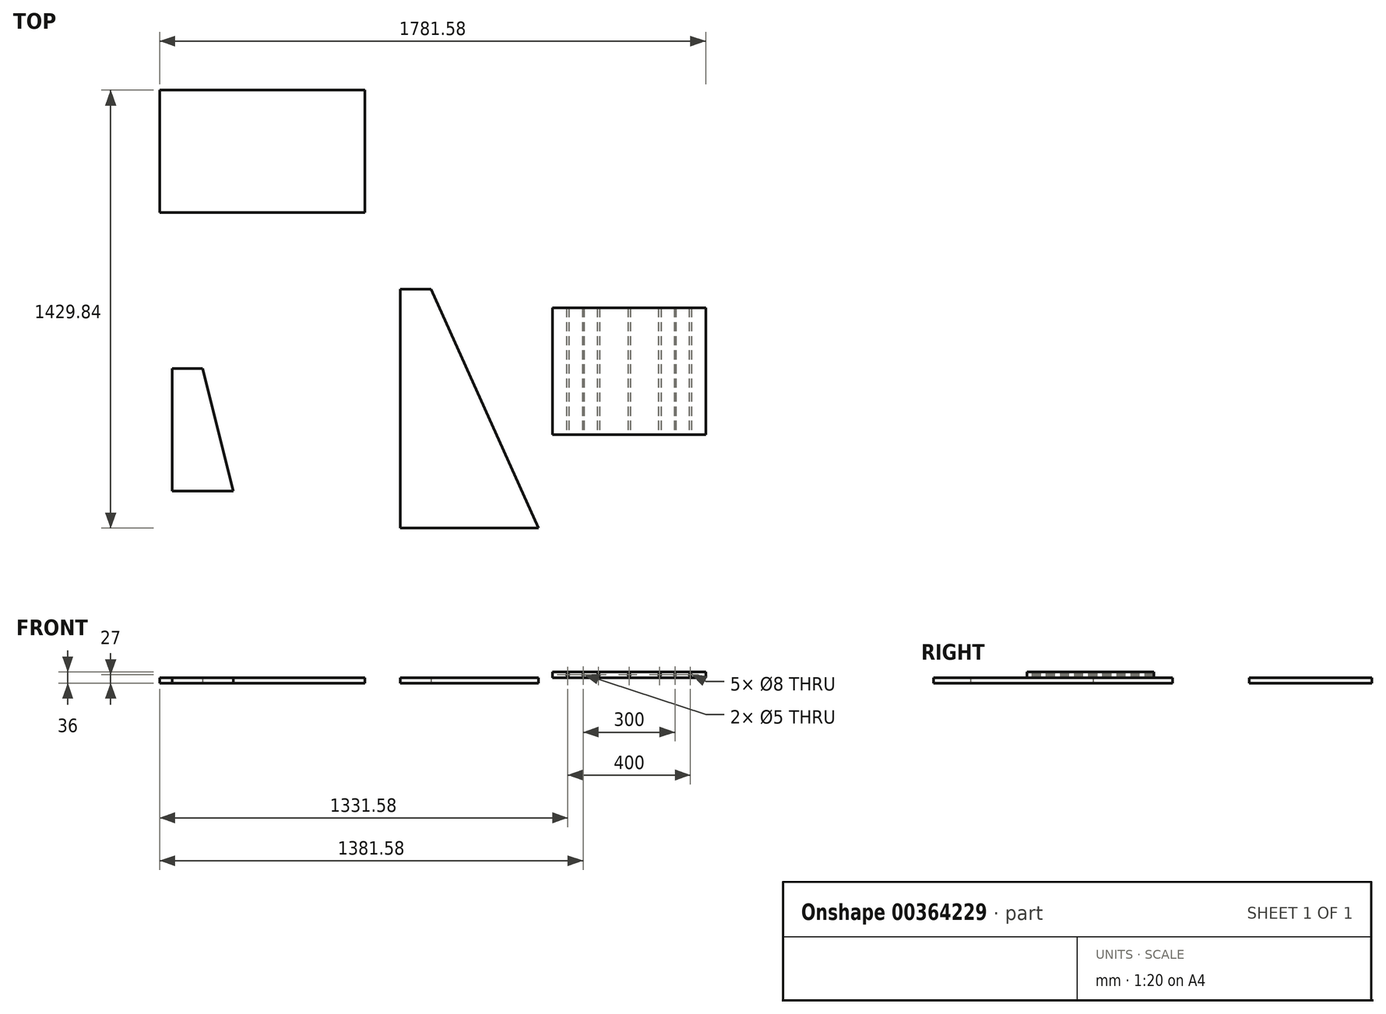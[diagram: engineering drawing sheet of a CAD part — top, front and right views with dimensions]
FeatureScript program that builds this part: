
annotation { "Feature Type Name" : "Feature", "Feature Type Description" : "" }
export const myFeature = defineFeature(function(context is Context, id is Id, definition is map)
    precondition{}
    {
        {
            var Q0;
            Q0=qCreatedBy(makeId("Top.planeOp"),FACE);
            var sketch = newSketch(context, id + "F0", { "sketchPlane" : qUnion([Q0])});
            skLineSegment(sketch, "E0.bottom", {"start": v(-196.07, -304.6) * mm, "end": v(253.93, -304.6) * mm});
            skLineSegment(sketch, "E0.top", {"start": v(-196.07, 475.4) * mm, "end": v(-96.07, 475.4) * mm});
            skLineSegment(sketch, "E0.left", {"start": v(-196.07, -304.6) * mm, "end": v(-196.07, 475.4) * mm});
            skLineSegment(sketch, "E0.right", {"start": v(253.93, -304.6) * mm, "end": v(-96.07, 475.4) * mm});
            skSolve(sketch);
        }
        {
            var Q0;
            Q0 = qSketchRegion(id + "F0", true);
            extrude(context, id + "F1", {"entities" : qUnion([Q0]), "depth" : 18 * mm});
        }
        {
            var Q0;
            Q0=makeQuery(id+"F1.opExtrude","CAP_FACE",FACE,{"disambiguationData":[OSD([sQuery(id+"F0.wireOp",EDGE,"E0.bottom"),sQuery(id+"F0.wireOp",EDGE,"E0.top"),sQuery(id+"F0.wireOp",EDGE,"E0.left"),sQuery(id+"F0.wireOp",EDGE,"E0.right")])],"isStart":false});
            var sketch = newSketch(context, id + "F2", { "sketchPlane" : qUnion([Q0])});
            skLineSegment(sketch, "E1.bottom", {"start": v(300, 414) * mm, "end": v(800, 414) * mm});
            skLineSegment(sketch, "E1.top", {"start": v(300, 0) * mm, "end": v(800, 0) * mm});
            skLineSegment(sketch, "E1.left", {"start": v(300, 414) * mm, "end": v(300, 0) * mm});
            skLineSegment(sketch, "E1.right", {"start": v(800, 414) * mm, "end": v(800, 0) * mm});
            skLineSegment(sketch, "E2", {"start": v(0, 0) * mm, "end": v(300, 0) * mm, "construction": true});
            skSolve(sketch);
        }
        {
            var Q0;
            {var subQ1=sQuery(id+"F2.wireOp",EDGE,"E1.bottom");Q0=makeQuery(id+"F2.imprint","IMPRINT",FACE,{"disambiguationData":[TD([[makeQuery(id+"F2.imprint","IMPRINT",EDGE,{"derivedFrom":subQ1}),-1.0]])]});}
            extrude(context, id + "F3", {"entities" : qUnion([Q0]), "depth" : 18 * mm});
        }
        {
            var Q0;
            Q0 = qSketchRegion(id + "F2", true);
            extrude(context, id + "F4", {"entities" : qUnion([Q0]), "operationType" : NewBodyOperationType.ADD, "depth" : 18 * mm});
        }
        {
            var Q0;
            Q0=makeQuery(id+"F3.opExtrude","SWEPT_FACE",FACE,{"disambiguationData":[OSD([sQuery(id+"F2.wireOp",EDGE,"E1.top")])]});
            var sketch = newSketch(context, id + "F5", { "sketchPlane" : qUnion([Q0])});
            skLineSegment(sketch, "E3", {"start": v(300, 27) * mm, "end": v(800, 27) * mm, "construction": true});
            skPoint(sketch, "E4", {"position": v(350, 27) * mm});
            skPoint(sketch, "E5.1.0.0", {"position": v(450, 27) * mm});
            skPoint(sketch, "E5.2.0.0", {"position": v(550, 27) * mm});
            skPoint(sketch, "E5.3.0.0", {"position": v(650, 27) * mm});
            skPoint(sketch, "E5.4.0.0", {"position": v(750, 27) * mm});
            skLineSegment(sketch, "E5.direction1", {"start": v(350, 27) * mm, "end": v(450, 27) * mm, "construction": true});
            skPoint(sketch, "E6", {"position": v(400, 27) * mm});
            skPoint(sketch, "E7", {"position": v(700, 27) * mm});
            skSolve(sketch);
        }
        {
            var Q0;
            Q0=sQuery(id+"F5.wireOp",VERTEX,"E4");
            var Q1;
            Q1=sQuery(id+"F5.wireOp",VERTEX,"E5.1.0.0");
            var Q2;
            Q2=sQuery(id+"F5.wireOp",VERTEX,"E5.2.0.0");
            var Q3;
            Q3=sQuery(id+"F5.wireOp",VERTEX,"E5.3.0.0");
            var Q4;
            Q4=sQuery(id+"F5.wireOp",VERTEX,"E5.4.0.0");
            var Q5;
            Q5=makeQuery(id+"F3.opExtrude","SWEPT_BODY",BODY,{"disambiguationData":[OSD([sQuery(id+"F2.wireOp",EDGE,"E1.bottom"),sQuery(id+"F2.wireOp",EDGE,"E1.top"),sQuery(id+"F2.wireOp",EDGE,"E1.left"),sQuery(id+"F2.wireOp",EDGE,"E1.right")])]});
            hole(context, id + "F6", {"style" : HoleStyle.SIMPLE, "endStyle" : HoleEndStyle.THROUGH, "holeDiameter" : 8 * mm, "isTappedThrough" : true, "tappedDepth" : 12 * mm, "tapClearance" : 3, "startFromSketch" : true, "locations" : qUnion([Q0, Q1, Q2, Q3, Q4]), "scope" : qUnion([Q5])});
        }
        {
            var Q0;
            Q0=qCreatedBy(makeId("Top.planeOp"),FACE);
            var sketch = newSketch(context, id + "F7", { "sketchPlane" : qUnion([Q0])});
            skLineSegment(sketch, "E8", {"start": v(-941.01, -183.88) * mm, "end": v(-941.01, 216.12) * mm});
            skLineSegment(sketch, "E9", {"start": v(-941.01, 216.12) * mm, "end": v(-841.01, 216.12) * mm});
            skLineSegment(sketch, "E10", {"start": v(-841.01, 216.12) * mm, "end": v(-741.01, -183.88) * mm});
            skLineSegment(sketch, "E11", {"start": v(-741.01, -183.88) * mm, "end": v(-941.01, -183.88) * mm});
            skSolve(sketch);
        }
        {
            var Q0;
            Q0 = qSketchRegion(id + "F7", true);
            extrude(context, id + "F8", {"entities" : qUnion([Q0]), "depth" : 18 * mm});
        }
        {
            var Q0;
            Q0=qCreatedBy(makeId("Top.planeOp"),FACE);
            var sketch = newSketch(context, id + "F9", { "sketchPlane" : qUnion([Q0])});
            skLineSegment(sketch, "E12.bottom", {"start": v(-981.58, 1125.24) * mm, "end": v(-311.58, 1125.24) * mm});
            skLineSegment(sketch, "E12.top", {"start": v(-981.58, 725.24) * mm, "end": v(-311.58, 725.24) * mm});
            skLineSegment(sketch, "E12.left", {"start": v(-981.58, 1125.24) * mm, "end": v(-981.58, 725.24) * mm});
            skLineSegment(sketch, "E12.right", {"start": v(-311.58, 1125.24) * mm, "end": v(-311.58, 725.24) * mm});
            skSolve(sketch);
        }
        {
            var Q0;
            Q0=makeQuery(id+"F9.imprint","IMPRINT",FACE,{"disambiguationData":[TD([[makeQuery(id+"F9.imprint","IMPRINT",EDGE,{"derivedFrom":sQuery(id+"F9.wireOp",EDGE,"E12.bottom")}),-1.0]])]});
            extrude(context, id + "F10", {"entities" : qUnion([Q0]), "depth" : 18 * mm});
        }
        {
            var Q0;
            Q0=sQuery(id+"F5.wireOp",VERTEX,"E6");
            var Q1;
            Q1=sQuery(id+"F5.wireOp",VERTEX,"E7");
            var Q2;
            Q2=makeQuery(id+"F3.opExtrude","SWEPT_BODY",BODY,{"disambiguationData":[OSD([sQuery(id+"F2.wireOp",EDGE,"E1.bottom"),sQuery(id+"F2.wireOp",EDGE,"E1.top"),sQuery(id+"F2.wireOp",EDGE,"E1.left"),sQuery(id+"F2.wireOp",EDGE,"E1.right")])]});
            hole(context, id + "F11", {"style" : HoleStyle.SIMPLE, "endStyle" : HoleEndStyle.THROUGH, "holeDiameter" : 5 * mm, "isTappedThrough" : true, "tappedDepth" : 12 * mm, "tapClearance" : 3, "startFromSketch" : true, "locations" : qUnion([Q0, Q1]), "scope" : qUnion([Q2])});
        }
    });
